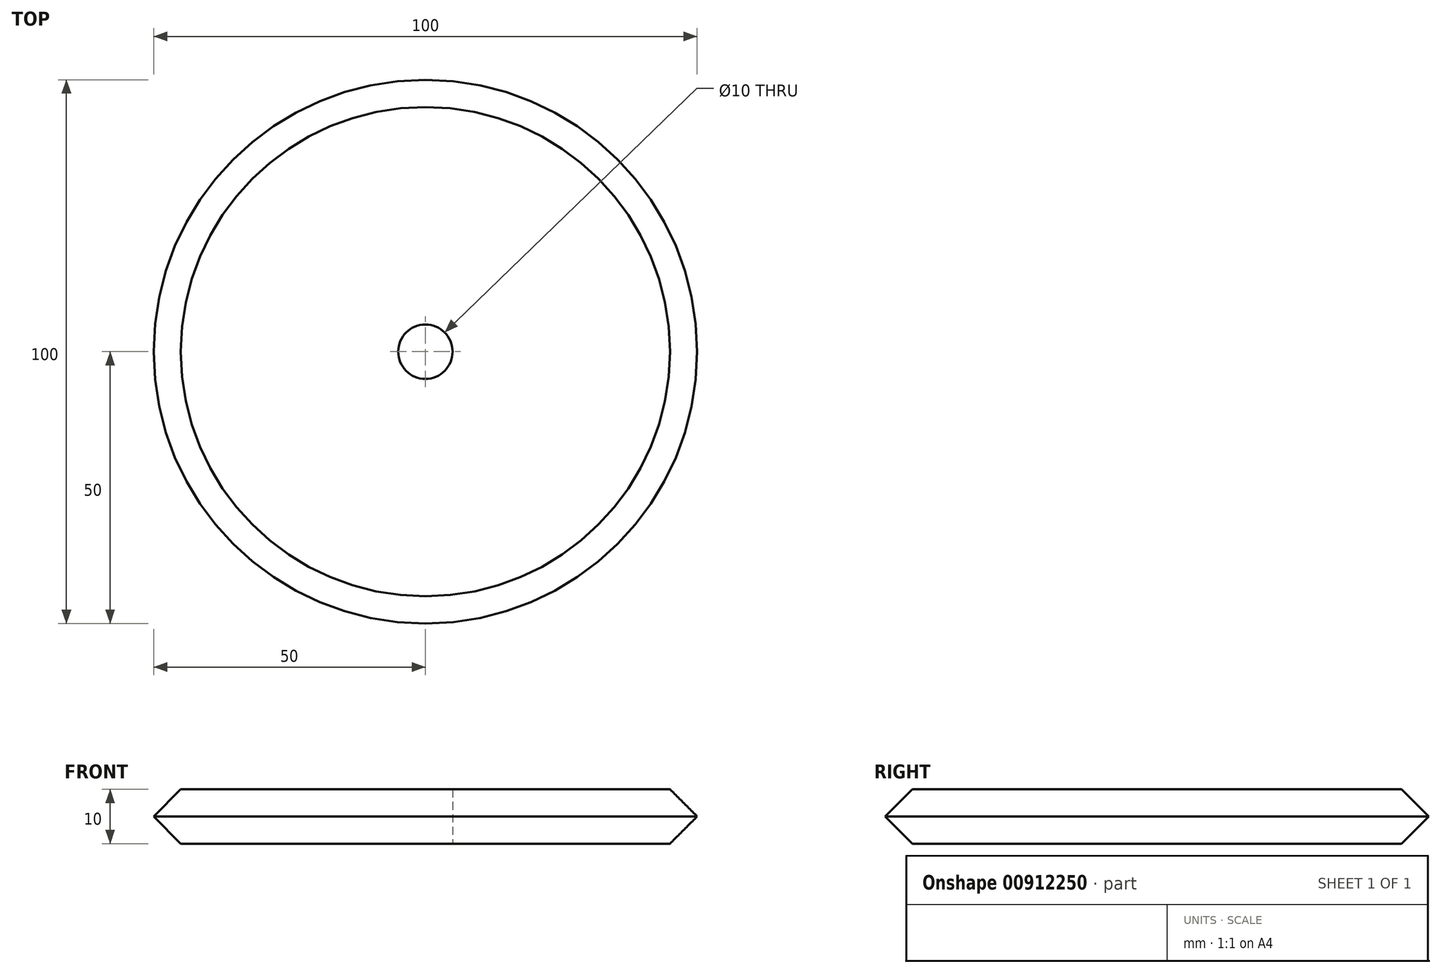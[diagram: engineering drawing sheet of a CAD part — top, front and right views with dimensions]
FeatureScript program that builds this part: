
annotation { "Feature Type Name" : "Feature", "Feature Type Description" : "" }
export const myFeature = defineFeature(function(context is Context, id is Id, definition is map)
    precondition{}
    {
        {
            var Q0;
            Q0=qCreatedBy(makeId("Top.planeOp"),FACE);
            var sketch = newSketch(context, id + "F0", { "sketchPlane" : qUnion([Q0])});
            skCircle(sketch, "E0", {"center": v(0, 0) * mm, "radius": 50 * mm});
            skCircle(sketch, "E1", {"center": v(0, 0) * mm, "radius": 40.07 * mm});
            skCircle(sketch, "E2", {"center": v(0, 0) * mm, "radius": 5 * mm});
            skSolve(sketch);
        }
        {
            var Q0;
            Q0=makeQuery(id+"F0.imprint","IMPRINT",FACE,{"disambiguationData":[TD([[makeQuery(id+"F0.imprint","IMPRINT",EDGE,{"derivedFrom":sQuery(id+"F0.wireOp",EDGE,"E0")}),1.0]])]});
            var Q1;
            Q1=makeQuery(id+"F0.imprint","IMPRINT",FACE,{"disambiguationData":[TD([[makeQuery(id+"F0.imprint","IMPRINT",EDGE,{"derivedFrom":sQuery(id+"F0.wireOp",EDGE,"E1")}),1.0]])]});
            extrude(context, id + "F1", {"entities" : qUnion([Q0, Q1]), "endBound" : BoundingType.SYMMETRIC, "depth" : 10 * mm, "offsetDistance" : 25.4 * mm});
        }
        {
            var Q0;
            Q0=makeQuery(id+"F1.opExtrude","CAP_EDGE",EDGE,{"disambiguationData":[OSD([sQuery(id+"F0.wireOp",EDGE,"E0")])],"isStart":false});
            var Q1;
            Q1=makeQuery(id+"F1.opExtrude","CAP_EDGE",EDGE,{"disambiguationData":[OSD([sQuery(id+"F0.wireOp",EDGE,"E0")])],"isStart":true});
            chamfer(context, id + "F2", {"entities" : qUnion([Q0, Q1]), "chamferType" : ChamferType.OFFSET_ANGLE, "width" : 5 * mm, "oppositeDirection" : false, "angle" : 45 * degree, "tangentPropagation" : true});
        }
    });
